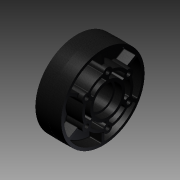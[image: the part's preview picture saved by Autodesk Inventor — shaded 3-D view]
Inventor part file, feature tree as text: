
AUTODESK INVENTOR PART (.ipt)
format: ipt  version: 2012 (Build 160160000, 160)  size: 1,138,688 bytes
history: native  units: in
note: dims shown in document units (in); Inventor stores cm internally (conversion verified against a paired STEP export)
features: fillet x2, imported_body x2, other x1
ambient origin geometry x8: Origin, YZ Plane, XZ Plane, XY Plane, X Axis, Y Axis, Z Axis, Center Point
feature tree (5):
  fillet  "Fillet10"  [1 undecoded]
  other  "4in 2013 Hub1"
  fillet  "Fillet9"  [1 undecoded]
  imported_body  "Base1"
  imported_body  "Base2"
note: 2 required parameter values undecoded (feature->parameter linkage not recoverable at this tier; creation-order binding heuristic only, values carry confidence <= 0.55)
